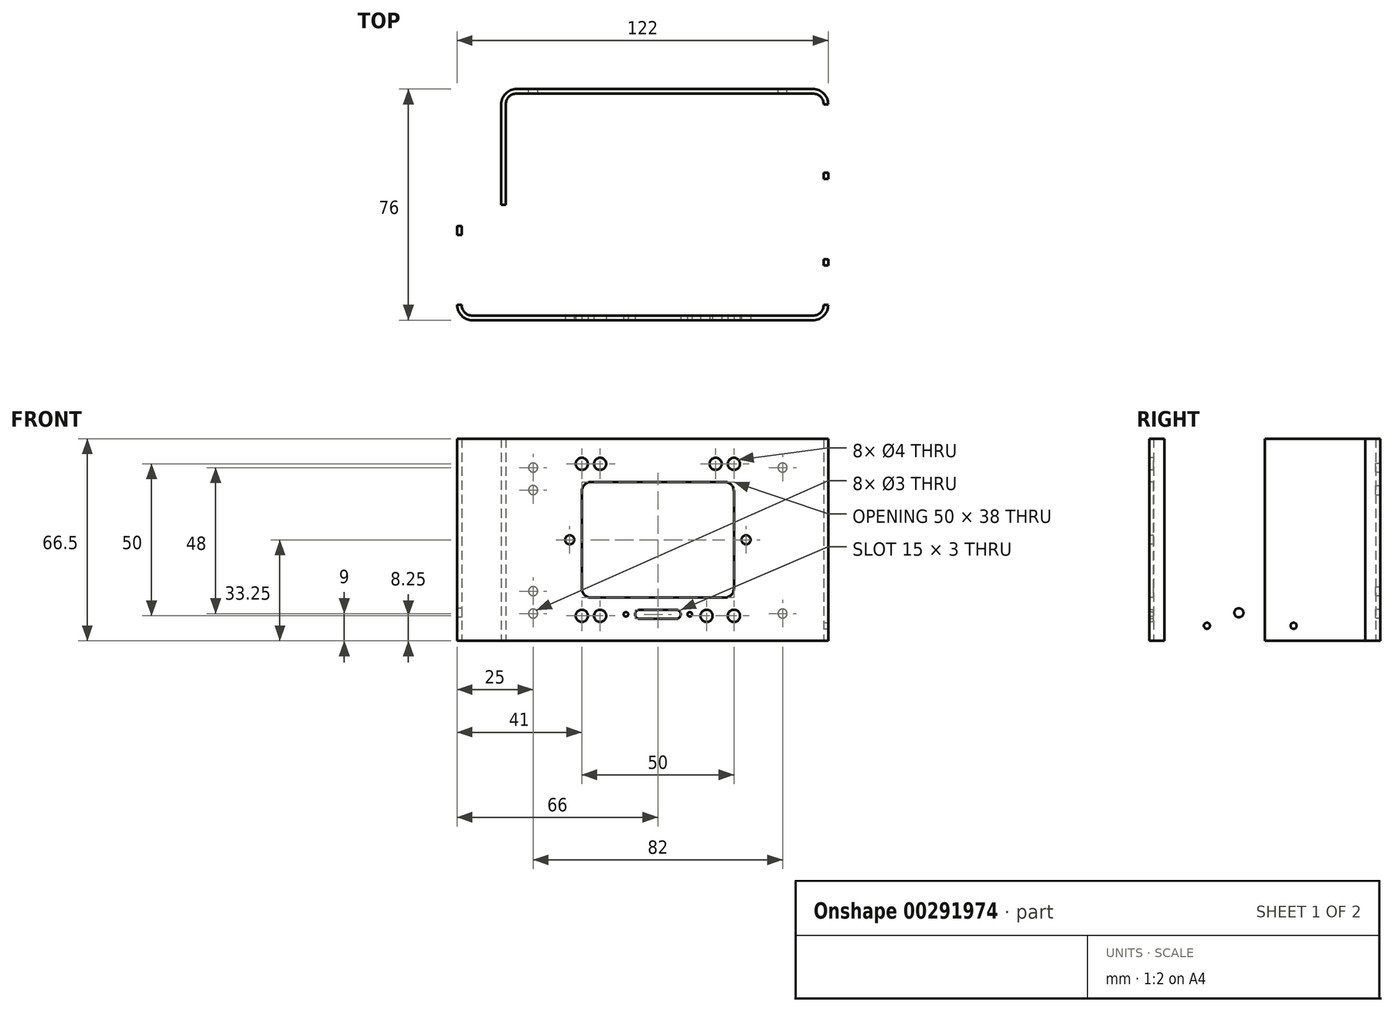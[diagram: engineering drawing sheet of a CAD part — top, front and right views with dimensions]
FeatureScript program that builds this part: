
annotation { "Feature Type Name" : "Feature", "Feature Type Description" : "" }
export const myFeature = defineFeature(function(context is Context, id is Id, definition is map)
    precondition{}
    {
        {
            var Q0;
            Q0=qCreatedBy(makeId("Top.planeOp"),FACE);
            var sketch = newSketch(context, id + "F0", { "sketchPlane" : qUnion([Q0])});
            skLineSegment(sketch, "E0", {"start": v(-64.5, 33) * mm, "end": v(-64.5, -33) * mm});
            skLineSegment(sketch, "E1", {"start": v(-61, -36.5) * mm, "end": v(51, -36.5) * mm});
            skLineSegment(sketch, "E2", {"start": v(54.5, -33) * mm, "end": v(54.5, 33) * mm});
            skLineSegment(sketch, "E3", {"start": v(51, 36.5) * mm, "end": v(-46.5, 36.5) * mm});
            skLineSegment(sketch, "E4", {"start": v(-50, 33) * mm, "end": v(-50, 0) * mm});
            skLineSegment(sketch, "E5.0", {"start": v(-51.5, 33) * mm, "end": v(-51.5, 0) * mm});
            skLineSegment(sketch, "E5.1", {"start": v(-66, 33) * mm, "end": v(-66, -33) * mm});
            skLineSegment(sketch, "E5.2", {"start": v(-61, -38) * mm, "end": v(51, -38) * mm});
            skLineSegment(sketch, "E5.3", {"start": v(56, -33) * mm, "end": v(56, 33) * mm});
            skLineSegment(sketch, "E5.4", {"start": v(51, 38) * mm, "end": v(-46.5, 38) * mm});
            skLineSegment(sketch, "E6", {"start": v(-50, 0) * mm, "end": v(-51.5, 0) * mm});
            skLineSegment(sketch, "E7", {"start": v(-64.5, 33) * mm, "end": v(-66, 33) * mm});
            skPoint(sketch, "E8.visualSharp", {"position": v(-64.5, -36.5) * mm});
            skArc(sketch, "E8.filletArc", {"start": v(-64.5, -33) * mm, "mid": v(-63.47, -35.47) * mm, "end": v(-61, -36.5) * mm});
            skPoint(sketch, "E9.visualSharp", {"position": v(54.5, -36.5) * mm});
            skArc(sketch, "E9.filletArc", {"start": v(51, -36.5) * mm, "mid": v(53.47, -35.47) * mm, "end": v(54.5, -33) * mm});
            skPoint(sketch, "E10.visualSharp", {"position": v(54.5, 36.5) * mm});
            skArc(sketch, "E10.filletArc", {"start": v(54.5, 33) * mm, "mid": v(53.47, 35.47) * mm, "end": v(51, 36.5) * mm});
            skPoint(sketch, "E11.visualSharp", {"position": v(-50, 36.5) * mm});
            skArc(sketch, "E11.filletArc", {"start": v(-46.5, 36.5) * mm, "mid": v(-48.97, 35.47) * mm, "end": v(-50, 33) * mm});
            skPoint(sketch, "E12.visualSharp", {"position": v(-66, -38) * mm});
            skArc(sketch, "E12.filletArc", {"start": v(-66, -33) * mm, "mid": v(-64.54, -36.54) * mm, "end": v(-61, -38) * mm});
            skPoint(sketch, "E13.visualSharp", {"position": v(56, -38) * mm});
            skArc(sketch, "E13.filletArc", {"start": v(51, -38) * mm, "mid": v(54.54, -36.54) * mm, "end": v(56, -33) * mm});
            skPoint(sketch, "E14.visualSharp", {"position": v(56, 38) * mm});
            skArc(sketch, "E14.filletArc", {"start": v(56, 33) * mm, "mid": v(54.54, 36.54) * mm, "end": v(51, 38) * mm});
            skPoint(sketch, "E15.visualSharp", {"position": v(-51.5, 38) * mm});
            skArc(sketch, "E15.filletArc", {"start": v(-46.5, 38) * mm, "mid": v(-50.04, 36.54) * mm, "end": v(-51.5, 33) * mm});
            skLineSegment(sketch, "E16", {"start": v(54.5, 0) * mm, "end": v(-12.48, 0) * mm, "construction": true});
            skLineSegment(sketch, "E17", {"start": v(2.25, 36.5) * mm, "end": v(-0.93, -15.16) * mm, "construction": true});
            skSolve(sketch);
        }
        {
            var Q0;
            Q0=qSketchRegion(id+"F0",true);
            extrude(context, id + "F1", {"entities" : qUnion([Q0]), "depth" : 66.5 * mm});
        }
        {
            var Q0;
            Q0=makeQuery(id+"F1.opExtrude","SWEPT_FACE",FACE,{"disambiguationData":[OSD([sQuery(id+"F0.wireOp",EDGE,"E5.2")])]});
            var sketch = newSketch(context, id + "F2", { "sketchPlane" : qUnion([Q0])});
            skLineSegment(sketch, "E18.bottom", {"start": v(-22, 52.25) * mm, "end": v(22, 52.25) * mm});
            skLineSegment(sketch, "E18.top", {"start": v(-22, 14.25) * mm, "end": v(22, 14.25) * mm});
            skLineSegment(sketch, "E18.left", {"start": v(-25, 49.25) * mm, "end": v(-25, 17.25) * mm});
            skLineSegment(sketch, "E18.right", {"start": v(25, 49.25) * mm, "end": v(25, 17.25) * mm});
            skLineSegment(sketch, "E19", {"start": v(-61, 33.25) * mm, "end": v(46, 33.25) * mm, "construction": true});
            skLineSegment(sketch, "E20", {"start": v(25, 33.25) * mm, "end": v(-25, 33.25) * mm, "construction": true});
            skPoint(sketch, "E21.visualSharp", {"position": v(-25, 52.25) * mm});
            skArc(sketch, "E21.filletArc", {"start": v(-22, 52.25) * mm, "mid": v(-24.12, 51.37) * mm, "end": v(-25, 49.25) * mm});
            skPoint(sketch, "E22.visualSharp", {"position": v(25, 52.25) * mm});
            skArc(sketch, "E22.filletArc", {"start": v(25, 49.25) * mm, "mid": v(24.12, 51.37) * mm, "end": v(22, 52.25) * mm});
            skPoint(sketch, "E23.visualSharp", {"position": v(25, 14.25) * mm});
            skArc(sketch, "E23.filletArc", {"start": v(22, 14.25) * mm, "mid": v(24.12, 15.13) * mm, "end": v(25, 17.25) * mm});
            skPoint(sketch, "E24.visualSharp", {"position": v(-25, 14.25) * mm});
            skArc(sketch, "E24.filletArc", {"start": v(-25, 17.25) * mm, "mid": v(-24.12, 15.13) * mm, "end": v(-22, 14.25) * mm});
            skCircle(sketch, "E25", {"center": v(-29, 33.25) * mm, "radius": 1.5 * mm});
            skCircle(sketch, "E26.MirrorC", {"center": v(29, 33.25) * mm, "radius": 1.5 * mm});
            skCircle(sketch, "E27", {"center": v(-25, 58.25) * mm, "radius": 2 * mm});
            skCircle(sketch, "E28.MirrorC", {"center": v(25, 58.25) * mm, "radius": 2 * mm});
            skCircle(sketch, "E29.MirrorC", {"center": v(-25, 8.25) * mm, "radius": 2 * mm});
            skCircle(sketch, "E30.MirrorC", {"center": v(25, 8.25) * mm, "radius": 2 * mm});
            skLineSegment(sketch, "E31.bottom", {"start": v(-6, 7.25) * mm, "end": v(6, 7.25) * mm});
            skPoint(sketch, "E32.visualSharp", {"position": v(7.5, 10.25) * mm});
            skLineSegment(sketch, "E31.top", {"start": v(-6, 10.25) * mm, "end": v(6, 10.25) * mm});
            skArc(sketch, "E33.filletArc", {"start": v(-6, 10.25) * mm, "mid": v(-7.06, 9.81) * mm, "end": v(-7.5, 8.75) * mm});
            skLineSegment(sketch, "E31.left", {"start": v(-7.5, 8.75) * mm, "end": v(-7.5, 8.75) * mm});
            skLineSegment(sketch, "E31.right", {"start": v(7.5, 8.75) * mm, "end": v(7.5, 8.75) * mm});
            skArc(sketch, "E34.filletArc", {"start": v(-7.5, 8.75) * mm, "mid": v(-7.06, 7.69) * mm, "end": v(-6, 7.25) * mm});
            skArc(sketch, "E35.filletArc", {"start": v(6, 7.25) * mm, "mid": v(7.06, 7.69) * mm, "end": v(7.5, 8.75) * mm});
            skArc(sketch, "E32.filletArc", {"start": v(7.5, 8.75) * mm, "mid": v(7.06, 9.81) * mm, "end": v(6, 10.25) * mm});
            skCircle(sketch, "E36", {"center": v(-10.5, 8.75) * mm, "radius": 0.75 * mm});
            skPoint(sketch, "E37", {"position": v(0, 10.25) * mm});
            skLineSegment(sketch, "E38", {"start": v(-10.5, 8.75) * mm, "end": v(8.14, 8.75) * mm, "construction": true});
            skPoint(sketch, "E33.visualSharp", {"position": v(-7.5, 10.25) * mm});
            skPoint(sketch, "E34.visualSharp", {"position": v(-7.5, 7.25) * mm});
            skPoint(sketch, "E35.visualSharp", {"position": v(7.5, 7.25) * mm});
            skLineSegment(sketch, "E39", {"start": v(0, 10.25) * mm, "end": v(0, 7.25) * mm, "construction": true});
            skCircle(sketch, "E40.MirrorC", {"center": v(10.5, 8.75) * mm, "radius": 0.75 * mm});
            skLineSegment(sketch, "E41", {"start": v(-25, 8.25) * mm, "end": v(-25, 58.25) * mm, "construction": true});
            skLineSegment(sketch, "E42", {"start": v(25, 58.25) * mm, "end": v(25, 8.25) * mm, "construction": true});
            skLineSegment(sketch, "E43", {"start": v(-25, 8.25) * mm, "end": v(25, 8.25) * mm, "construction": true});
            skLineSegment(sketch, "E44", {"start": v(25, 58.25) * mm, "end": v(-25, 58.25) * mm, "construction": true});
            skCircle(sketch, "E45", {"center": v(-19, 8.25) * mm, "radius": 2 * mm});
            skCircle(sketch, "E46.MirrorC", {"center": v(-19, 58.25) * mm, "radius": 2 * mm});
            skCircle(sketch, "E47.MirrorC", {"center": v(19, 58.25) * mm, "radius": 2 * mm});
            skCircle(sketch, "E48", {"center": v(16, 8.25) * mm, "radius": 2 * mm});
            skPoint(sketch, "E49", {"position": v(-61, 33.25) * mm});
            skSolve(sketch);
        }
        {
            var Q0;
            Q0=qSketchRegion(id+"F2",true);
            extrude(context, id + "F3", {"entities" : qUnion([Q0]), "operationType" : NewBodyOperationType.REMOVE, "oppositeDirection" : true, "depth" : 25 * mm});
        }
        {
            var Q0;
            Q0=makeQuery(id+"F1.opExtrude","SWEPT_FACE",FACE,{"disambiguationData":[OSD([sQuery(id+"F0.wireOp",EDGE,"E5.4")])]});
            var sketch = newSketch(context, id + "F4", { "sketchPlane" : qUnion([Q0])});
            skCircle(sketch, "E50", {"center": v(-41, 57) * mm, "radius": 1.5 * mm});
            skLineSegment(sketch, "E51", {"start": v(-41, 57) * mm, "end": v(-41, 9) * mm, "construction": true});
            skLineSegment(sketch, "E52", {"start": v(-41, 9) * mm, "end": v(41, 9) * mm, "construction": true});
            skLineSegment(sketch, "E53", {"start": v(41, 9) * mm, "end": v(41, 57) * mm, "construction": true});
            skLineSegment(sketch, "E54", {"start": v(41, 57) * mm, "end": v(-41, 57) * mm, "construction": true});
            skCircle(sketch, "E55", {"center": v(-41, 9) * mm, "radius": 1.5 * mm});
            skCircle(sketch, "E56", {"center": v(41, 9) * mm, "radius": 1.5 * mm});
            skCircle(sketch, "E57", {"center": v(41, 57) * mm, "radius": 1.5 * mm});
            skLineSegment(sketch, "E58", {"start": v(0, 1) * mm, "end": v(0, 113) * mm, "construction": true});
            skPoint(sketch, "E58.endSnap0", {"position": v(0, 1) * mm});
            skPoint(sketch, "E59", {"position": v(0, 57) * mm});
            skCircle(sketch, "E60", {"center": v(41, 49.63) * mm, "radius": 1.5 * mm});
            skCircle(sketch, "E61", {"center": v(41, 16.38) * mm, "radius": 1.5 * mm});
            skLineSegment(sketch, "E62", {"start": v(33.74, 33) * mm, "end": v(24.94, 33) * mm, "construction": true});
            skSolve(sketch);
        }
        {
            var Q0;
            Q0=makeQuery(id+"F4.imprint","IMPRINT",FACE,{"disambiguationData":[TD([[makeQuery(id+"F4.imprint","IMPRINT",EDGE,{"derivedFrom":sQuery(id+"F4.wireOp",EDGE,"E50")}),1.0]])]});
            var Q1;
            Q1=makeQuery(id+"F4.imprint","IMPRINT",FACE,{"disambiguationData":[TD([[makeQuery(id+"F4.imprint","IMPRINT",EDGE,{"derivedFrom":sQuery(id+"F4.wireOp",EDGE,"E55")}),1.0]])]});
            var Q2;
            Q2=makeQuery(id+"F4.imprint","IMPRINT",FACE,{"disambiguationData":[TD([[makeQuery(id+"F4.imprint","IMPRINT",EDGE,{"derivedFrom":sQuery(id+"F4.wireOp",EDGE,"E56")}),1.0]])]});
            var Q3;
            Q3=makeQuery(id+"F4.imprint","IMPRINT",FACE,{"disambiguationData":[TD([[makeQuery(id+"F4.imprint","IMPRINT",EDGE,{"derivedFrom":sQuery(id+"F4.wireOp",EDGE,"E57")}),1.0]])]});
            var Q4;
            Q4=makeQuery(id+"F4.imprint","IMPRINT",FACE,{"disambiguationData":[TD([[makeQuery(id+"F4.imprint","IMPRINT",EDGE,{"derivedFrom":sQuery(id+"F4.wireOp",EDGE,"E61")}),1.0]])]});
            var Q5;
            Q5=makeQuery(id+"F4.imprint","IMPRINT",FACE,{"disambiguationData":[TD([[makeQuery(id+"F4.imprint","IMPRINT",EDGE,{"derivedFrom":sQuery(id+"F4.wireOp",EDGE,"E60")}),1.0]])]});
            extrude(context, id + "F5", {"entities" : qUnion([Q0, Q1, Q2, Q3, Q4, Q5]), "operationType" : NewBodyOperationType.REMOVE, "oppositeDirection" : true, "depth" : 25 * mm});
        }
        {
            var Q0;
            Q0=makeQuery(id+"F1.opExtrude","SWEPT_FACE",FACE,{"disambiguationData":[OSD([sQuery(id+"F0.wireOp",EDGE,"E5.3")])]});
            var sketch = newSketch(context, id + "F6", { "sketchPlane" : qUnion([Q0])});
            skLineSegment(sketch, "E63.bottom", {"start": v(-21, 58.5) * mm, "end": v(-17, 58.5) * mm});
            skLineSegment(sketch, "E63.top", {"start": v(-21, 8) * mm, "end": v(-17, 8) * mm});
            skLineSegment(sketch, "E63.left", {"start": v(-24, 55.5) * mm, "end": v(-24, 11) * mm});
            skLineSegment(sketch, "E63.right", {"start": v(-14, 55.5) * mm, "end": v(-14, 11) * mm});
            skLineSegment(sketch, "E64.bottom", {"start": v(-5, 58.5) * mm, "end": v(24, 58.5) * mm});
            skLineSegment(sketch, "E64.top", {"start": v(-5, 8) * mm, "end": v(24, 8) * mm});
            skLineSegment(sketch, "E64.left", {"start": v(-8, 55.5) * mm, "end": v(-8, 11) * mm});
            skLineSegment(sketch, "E64.right", {"start": v(27, 55.5) * mm, "end": v(27, 11) * mm});
            skLineSegment(sketch, "E65", {"start": v(-14, 58.5) * mm, "end": v(-8, 58.5) * mm, "construction": true});
            skLineSegment(sketch, "E66", {"start": v(-14, 8) * mm, "end": v(-8, 8) * mm, "construction": true});
            skPoint(sketch, "E67.visualSharp", {"position": v(-24, 58.5) * mm});
            skArc(sketch, "E67.filletArc", {"start": v(-21, 58.5) * mm, "mid": v(-23.12, 57.62) * mm, "end": v(-24, 55.5) * mm});
            skPoint(sketch, "E68.visualSharp", {"position": v(-14, 58.5) * mm});
            skArc(sketch, "E68.filletArc", {"start": v(-14, 55.5) * mm, "mid": v(-14.88, 57.62) * mm, "end": v(-17, 58.5) * mm});
            skPoint(sketch, "E69.visualSharp", {"position": v(-24, 8) * mm});
            skArc(sketch, "E69.filletArc", {"start": v(-24, 11) * mm, "mid": v(-23.12, 8.88) * mm, "end": v(-21, 8) * mm});
            skPoint(sketch, "E70.visualSharp", {"position": v(-14, 8) * mm});
            skArc(sketch, "E70.filletArc", {"start": v(-17, 8) * mm, "mid": v(-14.88, 8.88) * mm, "end": v(-14, 11) * mm});
            skPoint(sketch, "E71.visualSharp", {"position": v(-8, 8) * mm});
            skArc(sketch, "E71.filletArc", {"start": v(-8, 11) * mm, "mid": v(-7.12, 8.88) * mm, "end": v(-5, 8) * mm});
            skPoint(sketch, "E72.visualSharp", {"position": v(27, 8) * mm});
            skArc(sketch, "E72.filletArc", {"start": v(24, 8) * mm, "mid": v(26.12, 8.88) * mm, "end": v(27, 11) * mm});
            skPoint(sketch, "E73.visualSharp", {"position": v(27, 58.5) * mm});
            skArc(sketch, "E73.filletArc", {"start": v(27, 55.5) * mm, "mid": v(26.12, 57.62) * mm, "end": v(24, 58.5) * mm});
            skPoint(sketch, "E74.visualSharp", {"position": v(-8, 58.5) * mm});
            skArc(sketch, "E74.filletArc", {"start": v(-5, 58.5) * mm, "mid": v(-7.12, 57.62) * mm, "end": v(-8, 55.5) * mm});
            skCircle(sketch, "E75", {"center": v(-19, 61.5) * mm, "radius": 1 * mm});
            skLineSegment(sketch, "E76", {"start": v(-24, 33.25) * mm, "end": v(27, 33.25) * mm, "construction": true});
            skLineSegment(sketch, "E77", {"start": v(-19, 58.5) * mm, "end": v(-19, 8) * mm, "construction": true});
            skPoint(sketch, "E77.endSnap0", {"position": v(-19, 8) * mm});
            skLineSegment(sketch, "E78", {"start": v(9.5, 8) * mm, "end": v(9.5, 58.5) * mm, "construction": true});
            skCircle(sketch, "E79", {"center": v(9.5, 61.5) * mm, "radius": 1 * mm});
            skCircle(sketch, "E80.MirrorC", {"center": v(-19, 5) * mm, "radius": 1 * mm});
            skCircle(sketch, "E81.MirrorC", {"center": v(9.5, 5) * mm, "radius": 1 * mm});
            skSolve(sketch);
        }
        {
            var Q0;
            Q0=makeQuery(id+"F6.imprint","IMPRINT",FACE,{"disambiguationData":[TD([[makeQuery(id+"F6.imprint","IMPRINT",EDGE,{"derivedFrom":sQuery(id+"F6.wireOp",EDGE,"E63.bottom")}),-1.0]])]});
            var Q1;
            Q1=makeQuery(id+"F6.imprint","IMPRINT",FACE,{"disambiguationData":[TD([[makeQuery(id+"F6.imprint","IMPRINT",EDGE,{"derivedFrom":sQuery(id+"F6.wireOp",EDGE,"E64.bottom")}),-1.0]])]});
            var Q2;
            Q2=makeQuery(id+"F6.imprint","IMPRINT",FACE,{"disambiguationData":[TD([[makeQuery(id+"F6.imprint","IMPRINT",EDGE,{"derivedFrom":sQuery(id+"F6.wireOp",EDGE,"E63.bottom")}),-1.0]])]});
            var Q3;
            Q3=makeQuery(id+"F6.imprint","IMPRINT",FACE,{"disambiguationData":[TD([[makeQuery(id+"F6.imprint","IMPRINT",EDGE,{"derivedFrom":sQuery(id+"F6.wireOp",EDGE,"E64.bottom")}),-1.0]])]});
            var Q4;
            Q4=makeQuery(id+"F6.imprint","IMPRINT",FACE,{"disambiguationData":[TD([[makeQuery(id+"F6.imprint","IMPRINT",EDGE,{"derivedFrom":sQuery(id+"F6.wireOp",EDGE,"E75")}),1.0]])]});
            var Q5;
            Q5=makeQuery(id+"F6.imprint","IMPRINT",FACE,{"disambiguationData":[TD([[makeQuery(id+"F6.imprint","IMPRINT",EDGE,{"derivedFrom":sQuery(id+"F6.wireOp",EDGE,"E79")}),1.0]])]});
            var Q6;
            Q6=makeQuery(id+"F6.imprint","IMPRINT",FACE,{"disambiguationData":[TD([[makeQuery(id+"F6.imprint","IMPRINT",EDGE,{"derivedFrom":sQuery(id+"F6.wireOp",EDGE,"E81.MirrorC")}),-1.0]])]});
            var Q7;
            Q7=makeQuery(id+"F6.imprint","IMPRINT",FACE,{"disambiguationData":[TD([[makeQuery(id+"F6.imprint","IMPRINT",EDGE,{"derivedFrom":sQuery(id+"F6.wireOp",EDGE,"E80.MirrorC")}),-1.0]])]});
            extrude(context, id + "F7", {"entities" : qUnion([Q0, Q1, Q2, Q3, Q4, Q5, Q6, Q7]), "operationType" : NewBodyOperationType.REMOVE, "oppositeDirection" : true, "depth" : 25 * mm});
        }
        {
            var Q0;
            Q0=makeQuery(id+"F1.opExtrude","SWEPT_FACE",FACE,{"disambiguationData":[OSD([sQuery(id+"F0.wireOp",EDGE,"E5.1")])]});
            var sketch = newSketch(context, id + "F8", { "sketchPlane" : qUnion([Q0])});
            skLineSegment(sketch, "E82", {"start": v(8.5, 66.5) * mm, "end": v(8.5, 0) * mm, "construction": true});
            skLineSegment(sketch, "E83.0.0", {"start": v(-33, 0) * mm, "end": v(33, 0) * mm});
            skLineSegment(sketch, "E83.0.1", {"start": v(33, 0) * mm, "end": v(33, 66.5) * mm});
            skLineSegment(sketch, "E83.0.2", {"start": v(33, 66.5) * mm, "end": v(-33, 66.5) * mm});
            skLineSegment(sketch, "E83.0.3", {"start": v(-33, 66.5) * mm, "end": v(-33, 0) * mm});
            skLineSegment(sketch, "E84", {"start": v(-33, 33.25) * mm, "end": v(33, 33.25) * mm, "construction": true});
            skCircle(sketch, "E85", {"center": v(8.5, 57.25) * mm, "radius": 1.5 * mm});
            skCircle(sketch, "E86.MirrorC", {"center": v(8.5, 9.25) * mm, "radius": 1.5 * mm});
            skSolve(sketch);
        }
        {
            var Q0;
            Q0=makeQuery(id+"F8.imprint","IMPRINT",FACE,{"disambiguationData":[TD([[makeQuery(id+"F8.imprint","IMPRINT",EDGE,{"derivedFrom":sQuery(id+"F8.wireOp",EDGE,"E85")}),1.0]])]});
            var Q1;
            Q1=makeQuery(id+"F8.imprint","IMPRINT",FACE,{"disambiguationData":[TD([[makeQuery(id+"F8.imprint","IMPRINT",EDGE,{"derivedFrom":sQuery(id+"F8.wireOp",EDGE,"E86.MirrorC")}),-1.0]])]});
            extrude(context, id + "F9", {"entities" : qUnion([Q0, Q1]), "operationType" : NewBodyOperationType.REMOVE, "oppositeDirection" : true, "depth" : 1.5 * mm});
        }
    });
